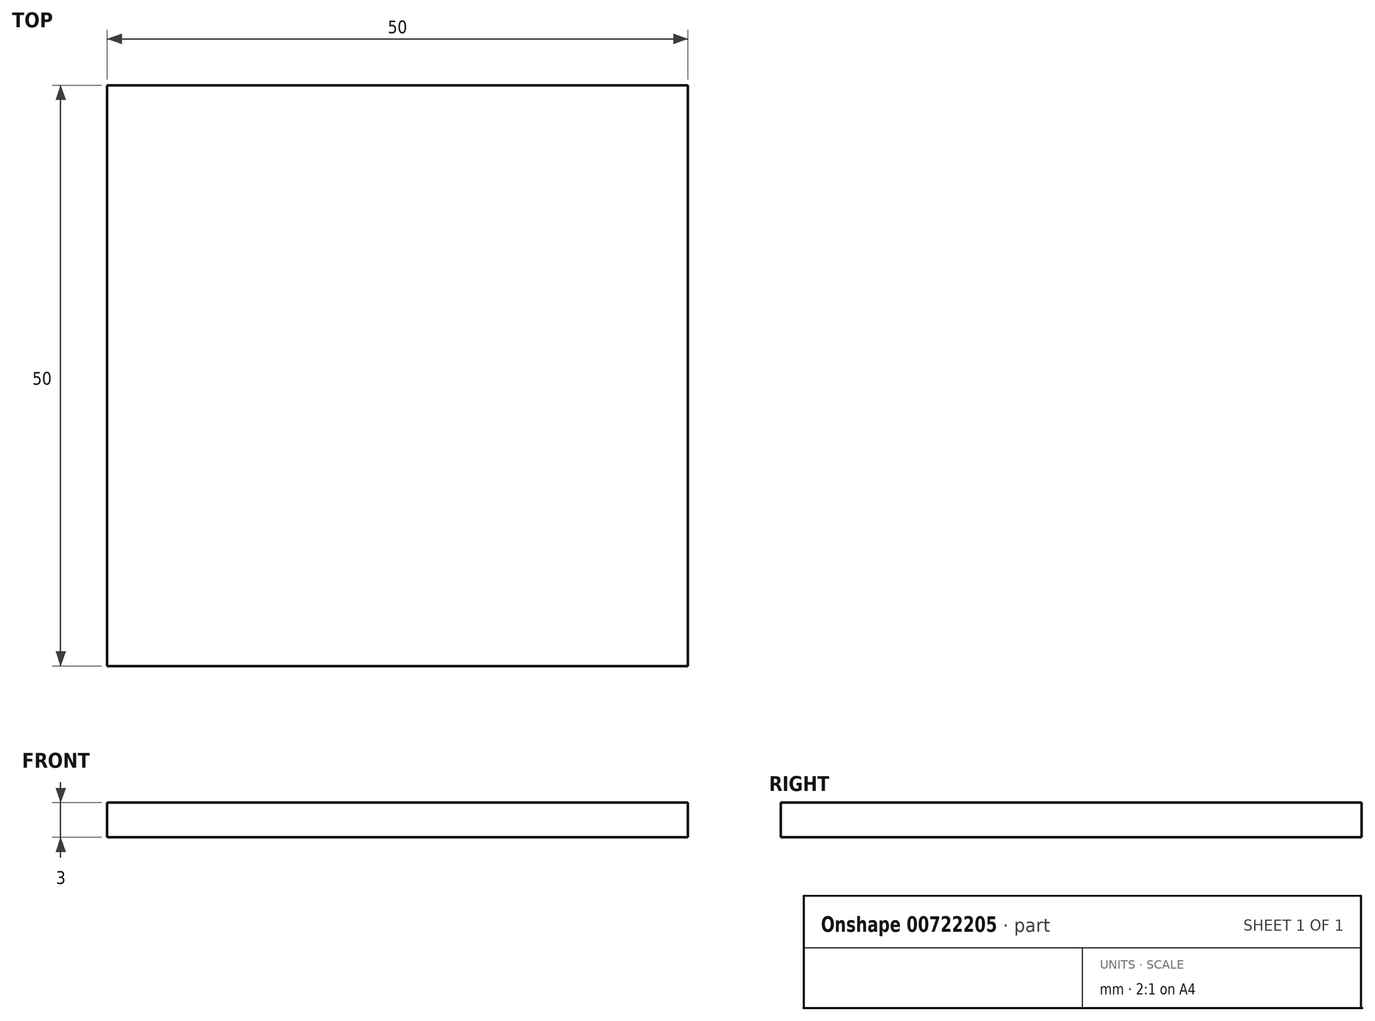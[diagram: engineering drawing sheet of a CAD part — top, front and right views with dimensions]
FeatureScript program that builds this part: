
annotation { "Feature Type Name" : "Feature", "Feature Type Description" : "" }
export const myFeature = defineFeature(function(context is Context, id is Id, definition is map)
    precondition{}
    {
        {
            var Q0;
            Q0=qCreatedBy(makeId("Top.planeOp"),FACE);
            var sketch = newSketch(context, id + "F0", { "sketchPlane" : qUnion([Q0])});
            skLineSegment(sketch, "E0", {"start": v(-44.25, -5.28) * mm, "end": v(-44.25, -55.28) * mm});
            skLineSegment(sketch, "E1", {"start": v(-44.25, -55.28) * mm, "end": v(5.75, -55.28) * mm});
            skLineSegment(sketch, "E2", {"start": v(5.75, -55.28) * mm, "end": v(5.75, -5.28) * mm});
            skLineSegment(sketch, "E3", {"start": v(-44.25, -5.28) * mm, "end": v(5.75, -5.28) * mm});
            skSolve(sketch);
        }
        {
            var Q0;
            Q0=makeQuery(id+"F0.imprint","IMPRINT",FACE,{"disambiguationData":[TD([[makeQuery(id+"F0.imprint","IMPRINT",EDGE,{"derivedFrom":sQuery(id+"F0.wireOp",EDGE,"E0")}),1.0]])]});
            extrude(context, id + "F1", {"entities" : qUnion([Q0]), "depth" : 3 * mm, "offsetDistance" : 25 * mm});
        }
    });
